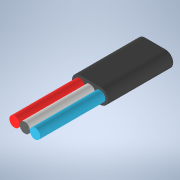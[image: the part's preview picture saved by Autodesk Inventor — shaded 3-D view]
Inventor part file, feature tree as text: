
AUTODESK INVENTOR PART (.ipt)
format: ipt  version: 2022 (Build 260153000, 153)  size: 116,736 bytes
history: native  units: in
note: dims shown in document units (in); Inventor stores cm internally (conversion verified against a paired STEP export)
features: extrude x2, sketch x2
ambient origin geometry x8: Origin, YZ Plane, XZ Plane, XY Plane, X Axis, Y Axis, Z Axis, Center Point
bodies: Solid1 (feature_tree)
feature tree (4):
  extrude  "Extrusion1"  Depth=0.0591in
  extrude  "Extrusion2"  Depth=0.0787in
  sketch  "Sketch1"  dims[d0=0.1575in d1=0.0591in]
  sketch  "Sketch2"  dims[d2=0.75in d3=0.0in d4=0.0787in d5=0.0787in d6=0.0787in d7=0.5in d8=0.0in]
